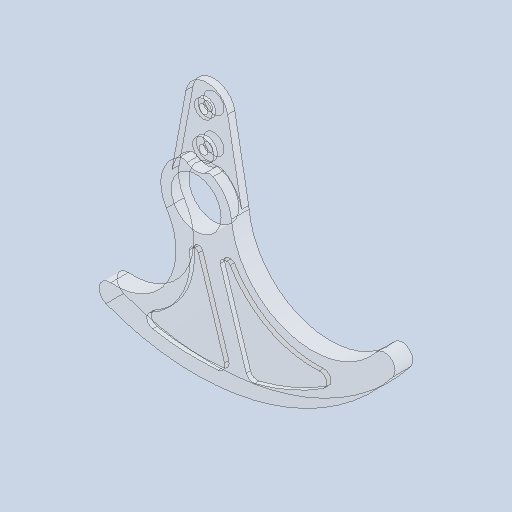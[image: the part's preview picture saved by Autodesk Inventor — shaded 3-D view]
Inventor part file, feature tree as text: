
AUTODESK INVENTOR PART (.ipt)
format: ipt  version: 2023 (Build 270158000, 158)  size: 207,360 bytes
history: native  units: mm
features: other x3, sketch x2
ambient origin geometry x8: Origin, YZ Plane, XZ Plane, XY Plane, X Axis, Y Axis, Z Axis, Center Point
bodies: Solid2 (feature_tree)
feature tree (5):
  other  "ヘッケン.ipt"
  other  "Solid2::ヘッケン.ipt"
  other  "TaggingFeature1"
  sketch  "Sketch1"  dims[d0=10.0mm]
  sketch  "スケッチ5"
